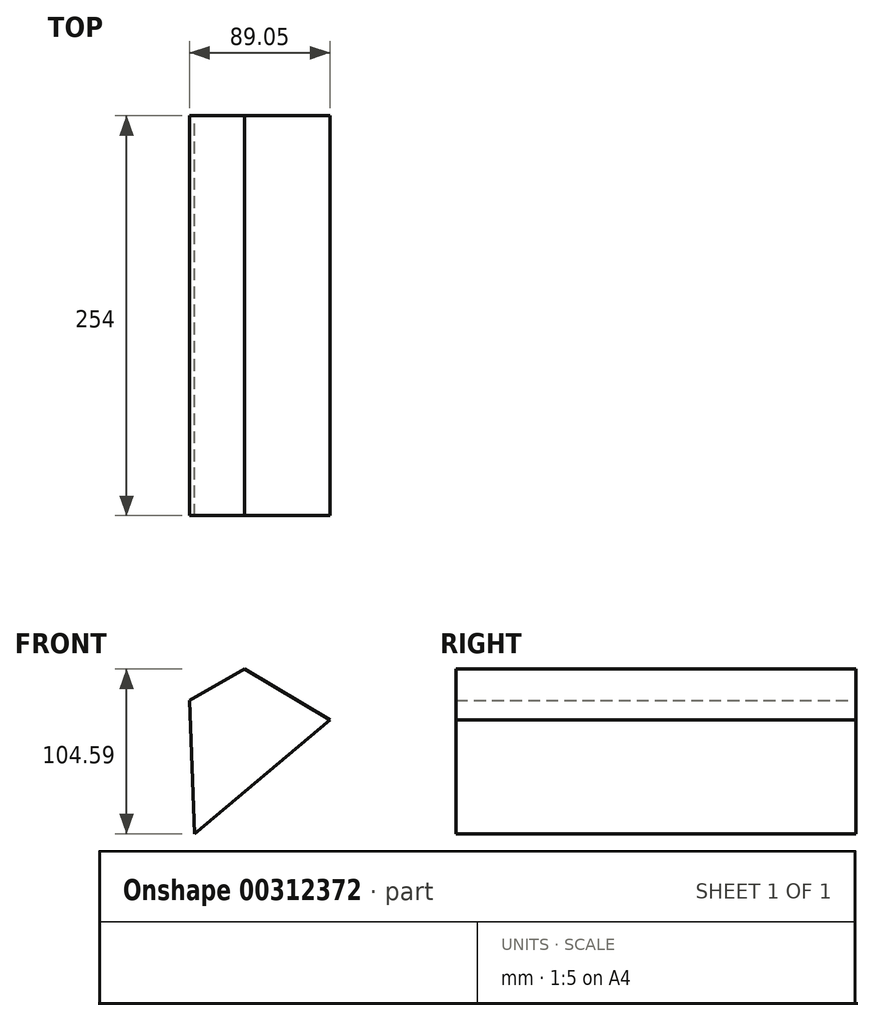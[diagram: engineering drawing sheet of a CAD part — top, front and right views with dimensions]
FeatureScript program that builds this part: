
annotation { "Feature Type Name" : "Feature", "Feature Type Description" : "" }
export const myFeature = defineFeature(function(context is Context, id is Id, definition is map)
    precondition{}
    {
        {
            var Q0;
            Q0=qCreatedBy(makeId("Front.planeOp"),FACE);
            var sketch = newSketch(context, id + "F0", { "sketchPlane" : qUnion([Q0])});
            skLineSegment(sketch, "E0", {"start": v(-59.2, 48.23) * mm, "end": v(-24.46, 68.04) * mm});
            skLineSegment(sketch, "E1", {"start": v(-24.46, 68.04) * mm, "end": v(29.85, 35.77) * mm});
            skLineSegment(sketch, "E2", {"start": v(29.85, 35.77) * mm, "end": v(-56.27, -36.55) * mm});
            skLineSegment(sketch, "E3", {"start": v(-56.27, -36.55) * mm, "end": v(-59.2, 48.23) * mm});
            skSolve(sketch);
        }
        {
            var Q0;
            Q0=makeQuery(id+"F0.imprint","IMPRINT",FACE,{"disambiguationData":[TD([[makeQuery(id+"F0.imprint","IMPRINT",EDGE,{"derivedFrom":sQuery(id+"F0.wireOp",EDGE,"E0")}),-1.0]])]});
            extrude(context, id + "F1", {"entities" : qUnion([Q0]), "depth" : 254 * mm});
        }
    });
